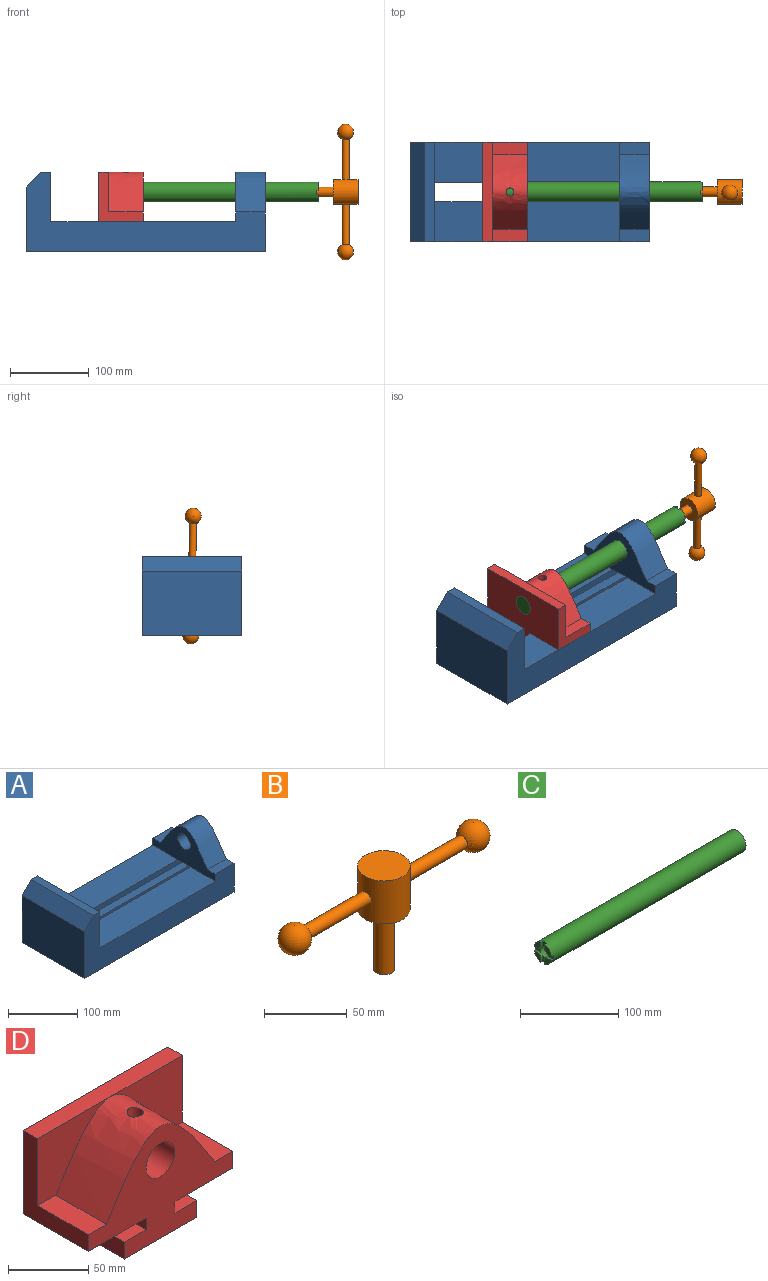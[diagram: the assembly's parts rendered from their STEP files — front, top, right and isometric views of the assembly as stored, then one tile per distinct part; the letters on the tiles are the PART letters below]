
ASSEMBLY  parts=4 mates=3
PART A: 26 faces, bbox 304.8x127x104.2 mm
  f0: plane 127x104.25mm, normal (1,0,0), area 7517.4mm2, adj f2,f8,f9,f11,f12,f13,f14,f15
  f1: plane 127x66.15mm, normal (-1,0,0), area 4130.4mm2, adj f3,f6,f8,f9,f11,f22,f23,f24
  f2: plane 304.8x127mm, normal (0,0,-1), area 31774.1mm2, adj f0,f5,f7,f8,f9,f13,f14
  f3: plane 234.95x50.8mm, normal (0,0,1), area 11935.5mm2, adj f1,f7,f8,f18
  f4: plane 127x12.7mm, normal (0,0,1), area 1612.9mm2, adj f7,f8,f9,f10
  f5: plane 127x82.55mm, normal (-1,0,0), area 10483.8mm2, adj f2,f8,f9,f10
  f6: plane 234.95x50.8mm, normal (0,0,1), area 11935.5mm2, adj f1,f7,f9,f19
  f7: plane 127x101.6mm, normal (1,0,0), area 9516.1mm2, adj f2,f3,f4,f6,f8,f9,f12,f13
  f8: plane 304.8x101.6mm, normal (0,1,0), area 13931.4mm2, adj f0,f1,f2,f3,f4,f5,f7,f10
  f9: plane 304.8x101.6mm, normal (0,-1,0), area 13931.4mm2, adj f0,f1,f2,f4,f5,f6,f7,f10
  f10: plane 127x19.05mm, normal (-0.71,0,0.71), area 3421.5mm2, adj f4,f5,f8,f9
  f11: plane 38.1x25.4mm, normal (0,0,-1), area 967.7mm2, adj f0,f1,f18,f19
  f12: plane 273.05x19.05mm, normal (0,0,1), area 5201.6mm2, adj f0,f7,f13,f21
  f13: plane 273.05x16.51mm, normal (0,1,0), area 4508.1mm2, adj f0,f2,f7,f12
  f14: plane 273.05x16.51mm, normal (0,-1,0), area 4508.1mm2, adj f0,f2,f7,f15
  f15: plane 273.05x19.05mm, normal (0,0,1), area 5201.6mm2, adj f0,f7,f14,f16
  f16: plane 273.05x12.7mm, normal (0,-1,0), area 3467.7mm2, adj f0,f7,f15,f17
  f17: plane 273.05x19.05mm, normal (0,0,-1), area 5201.6mm2, adj f0,f7,f16,f18
  f18: plane 273.05x8.89mm, normal (0,-1,0), area 2427.4mm2, adj f0,f3,f7,f11,f17
  f19: plane 273.05x8.89mm, normal (0,1,0), area 2427.4mm2, adj f0,f6,f7,f11,f20
  f20: plane 273.05x19.05mm, normal (0,0,-1), area 5201.6mm2, adj f0,f7,f19,f21
  f21: plane 273.05x12.7mm, normal (0,1,0), area 3467.7mm2, adj f0,f7,f12,f20
  f22: plane 38.1x15.88mm, normal (0,0,1), area 604.8mm2, adj f0,f1,f9,f23
  f23: extruded ~95.25x50.8mm, area 5470.6mm2, adj f0,f1,f22,f25
  f24: cylinder r=12.7mm len=38.1mm, axis (1,0,0), area 3040.2mm2, adj f0,f1
  f25: plane 38.1x15.88mm, normal (0,0,1), area 604.8mm2, adj f0,f1,f8,f23
PART B: 9 faces, bbox 172.7x31.8x76.2 mm
  f0: cylinder r=15.88mm len=31.75mm, axis (0,0,-1), area 3041.4mm2, adj f3,f4,f5,f6
  f1: cylinder r=6.35mm len=44.45mm, axis (0,0,1), area 1773.5mm2, adj f2,f4
  f2: plane 12.7x12.7mm, normal (0,0,-1), area 126.7mm2, adj f1
  f3: plane 31.75x31.75mm, normal (0,0,1), area 791.7mm2, adj f0
  f4: plane 31.75x31.75mm, normal (0,0,-1), area 665.1mm2, adj f0,f1
  f5: cylinder r=4.45mm len=51.82mm, axis (-1,0,0), area 1438.5mm2, adj f0,f8
  f6: cylinder r=4.45mm len=51.82mm, axis (-1,0,0), area 1438.5mm2, adj f0,f7
  f7: sphere r=10.16mm, area 1231.8mm2, adj f6
  f8: sphere r=10.16mm, area 1231.8mm2, adj f5
PART C: 20 faces, bbox 279.4x25.4x25.4 mm
  f0: plane 9.93x9.67mm, normal (-1,0,0), area 61.1mm2, adj f3,f4,f16,f18
  f1: plane 10.14x9.88mm, normal (-1,0,0), area 63.5mm2, adj f3,f4,f10,f12
  f2: plane 10.17x10.03mm, normal (-1,0,0), area 64.5mm2, adj f3,f4,f9,f19
  f3: cylinder r=12.7mm len=279.4mm, axis (-1,0,0), area 22243.2mm2, adj f0,f1,f2,f5,f6,f8,f9,f10
  f4: cylinder r=6.35mm len=25.4mm, axis (-1,0,0), area 960.3mm2, adj f0,f1,f2,f5,f7,f8,f9,f10
  f5: plane 9.77x9.63mm, normal (-1,0,0), area 60.1mm2, adj f3,f4,f13,f15
  f6: plane 25.4x25.4mm, normal (1,0,0), area 506.7mm2, adj f3
  f7: plane 12.7x12.7mm, normal (-1,0,0), area 126.7mm2, adj f4
  f8: plane 6.91x5.08mm, normal (-1,0,0), area 32.7mm2, adj f3,f4,f9,f10
  f9: plane 6.61x2.54mm, normal (0,-1,0), area 16.8mm2, adj f2,f3,f4,f8
  f10: plane 6.64x2.54mm, normal (0,1,0), area 16.9mm2, adj f1,f3,f4,f8
  f11: plane 7x5.08mm, normal (-1,0,0), area 32.7mm2, adj f3,f4,f12,f13
  f12: plane 6.57x2.54mm, normal (0,0,-1), area 16.7mm2, adj f1,f3,f4,f11
  f13: plane 6.69x2.54mm, normal (0,0,1), area 17mm2, adj f3,f4,f5,f11
  f14: plane 6.91x5.08mm, normal (-1,0,0), area 32.7mm2, adj f3,f4,f15,f16
  f15: plane 6.64x2.54mm, normal (0,1,0), area 16.9mm2, adj f3,f4,f5,f14
  f16: plane 6.61x2.54mm, normal (0,-1,0), area 16.8mm2, adj f0,f3,f4,f14
  f17: plane 7x5.08mm, normal (-1,0,0), area 32.7mm2, adj f3,f4,f18,f19
  f18: plane 6.69x2.54mm, normal (0,0,1), area 17mm2, adj f0,f3,f4,f17
  f19: plane 6.57x2.54mm, normal (0,0,-1), area 16.7mm2, adj f2,f3,f4,f17
PART D: 21 faces, bbox 127x57.2x87.7 mm
  f0: plane 63.5x57.15mm, normal (1,0,0), area 1371mm2, adj f3,f4,f5,f6,f17,f18
  f1: plane 63.5x57.15mm, normal (-1,0,0), area 1371mm2, adj f3,f4,f5,f11,f19,f20
  f2: plane 63.5x57.15mm, normal (0,0,-1), area 3629mm2, adj f3,f4,f9,f12
  f3: plane 127x85.09mm, normal (0,1,0), area 8590mm2, adj f0,f1,f2,f5,f6,f7,f8,f9
  f4: plane 127x87.74mm, normal (0,-1,0), area 5162.7mm2, adj f0,f1,f2,f6,f7,f8,f9,f10
  f5: plane 127x12.7mm, normal (0,0,1), area 1612.9mm2, adj f0,f1,f3,f18,f20
  f6: plane 57.15x50.8mm, normal (0,0,-1), area 2903.2mm2, adj f0,f3,f4,f7
  f7: plane 57.15x8.89mm, normal (1,0,0), area 508.1mm2, adj f3,f4,f6,f8
  f8: plane 57.15x19.05mm, normal (0,0,1), area 1088.7mm2, adj f3,f4,f7,f9
  f9: plane 57.15x12.7mm, normal (1,0,0), area 725.8mm2, adj f2,f3,f4,f8
  f10: plane 57.15x8.89mm, normal (-1,0,0), area 508.1mm2, adj f3,f4,f11,f13
  f11: plane 57.15x50.8mm, normal (0,0,-1), area 2903.2mm2, adj f1,f3,f4,f10
  f12: plane 57.15x12.7mm, normal (-1,0,0), area 725.8mm2, adj f2,f3,f4,f13
  f13: plane 57.15x19.05mm, normal (0,0,1), area 1088.7mm2, adj f3,f4,f10,f12
  f14: cylinder r=12.7mm len=57.15mm, axis (0,-1,0), area 4477.5mm2, adj f3,f4,f15
  f15: cylinder r=5.08mm len=13.76mm, axis (0,0,1), area 408.7mm2, adj f14,f16
  f16: extruded ~95.25x50.8mm, area 6300mm2, adj f4,f15,f17,f18,f19,f20
  f17: plane 44.45x15.88mm, normal (0,0,1), area 705.6mm2, adj f0,f4,f16,f18
  f18: plane 66.15x53.45mm, normal (0,-1,0), area 1713.7mm2, adj f0,f5,f16,f17
  f19: plane 44.45x15.88mm, normal (0,0,1), area 705.6mm2, adj f1,f4,f16,f20
  f20: plane 66.15x53.45mm, normal (0,-1,0), area 1713.7mm2, adj f1,f5,f16,f19
PLACE A t=(22.61,43.41,-9.14)mm fixed
PLACE B rot(axis=(-0.71,0.01,-0.71),179.2deg) t=(413.41,106.91,67.06)mm
PLACE C rot(axis=(0,-0.01,1),180deg) t=(394.36,119.86,54.62)mm
PLACE D rot(axis=(0,0,1),90deg) t=(172.11,43.41,7.37)mm
MATE revolute D.f14 <-> C.f3  axis (-1,0,0) through (114.96,106.91,67.06)mm
MATE fastened B.f0 <-> C.f3  axis (1,0,0) through (368.96,106.91,67.06)mm
MATE slider A.f24 <-> D.f14  axis (1,0,0) through (289.31,106.91,67.06)mm
